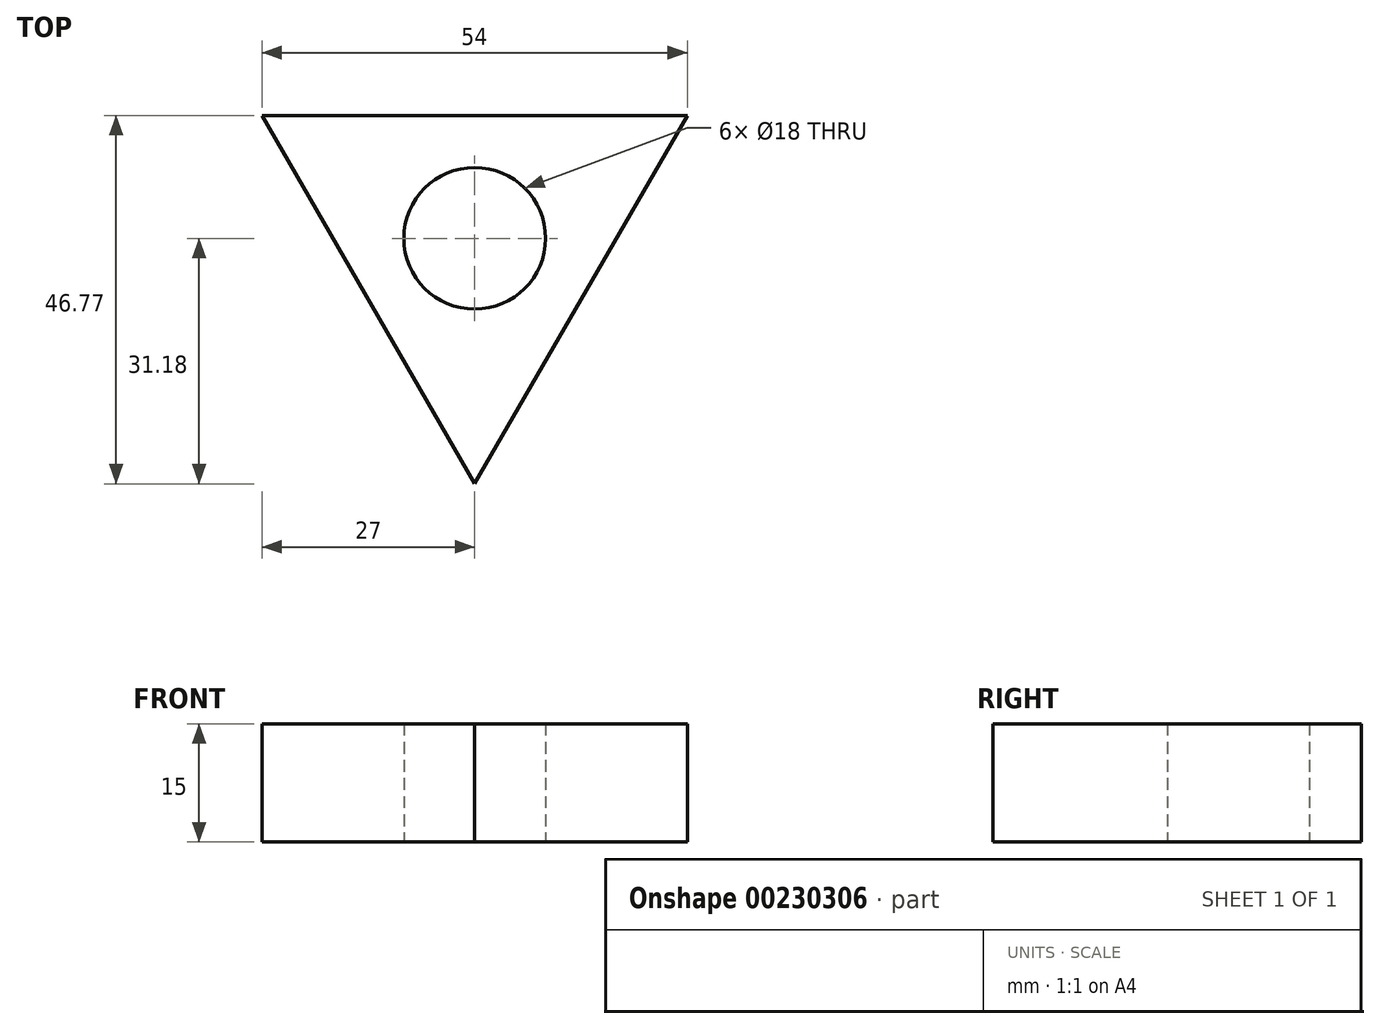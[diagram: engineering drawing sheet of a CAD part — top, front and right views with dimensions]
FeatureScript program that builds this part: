
annotation { "Feature Type Name" : "Feature", "Feature Type Description" : "" }
export const myFeature = defineFeature(function(context is Context, id is Id, definition is map)
    precondition{}
    {
        {
            var Q0;
            Q0=qCreatedBy(makeId("Top.planeOp"),FACE);
            var sketch = newSketch(context, id + "F0", { "sketchPlane" : qUnion([Q0])});
            skCircle(sketch, "E0.cCircle", {"center": v(0, 0) * mm, "radius": 15.59 * mm, "construction": true});
            skLineSegment(sketch, "E0.0", {"start": v(-27, 15.59) * mm, "end": v(27, 15.59) * mm});
            skLineSegment(sketch, "E0.1", {"start": v(27, 15.59) * mm, "end": v(0, -31.18) * mm});
            skLineSegment(sketch, "E0.2", {"start": v(0, -31.18) * mm, "end": v(-27, 15.59) * mm});
            skPoint(sketch, "E0.0.midPoint", {"position": v(0, 15.59) * mm});
            skSolve(sketch);
        }
        {
            var Q0;
            Q0=qCreatedBy(makeId("Top.planeOp"),FACE);
            var sketch = newSketch(context, id + "F1", { "sketchPlane" : qUnion([Q0])});
            skCircle(sketch, "E1", {"center": v(0, 0) * mm, "radius": 9 * mm});
            skSolve(sketch);
        }
        {
            var Q0;
            Q0=makeQuery(id+"F0.imprint","IMPRINT",FACE,{"disambiguationData":[TD([[makeQuery(id+"F0.imprint","IMPRINT",EDGE,{"derivedFrom":sQuery(id+"F0.wireOp",EDGE,"E0.0")}),-1.0]])]});
            extrude(context, id + "F2", {"entities" : qUnion([Q0]), "depth" : 15 * mm});
        }
        {
            var Q0;
            Q0=makeQuery(id+"F1.imprint","IMPRINT",FACE,{"disambiguationData":[TD([[makeQuery(id+"F1.imprint","IMPRINT",EDGE,{"derivedFrom":sQuery(id+"F1.wireOp",EDGE,"E1")}),1.0]])]});
            extrude(context, id + "F3", {"entities" : qUnion([Q0]), "operationType" : NewBodyOperationType.REMOVE, "depth" : 15 * mm});
        }
    });
